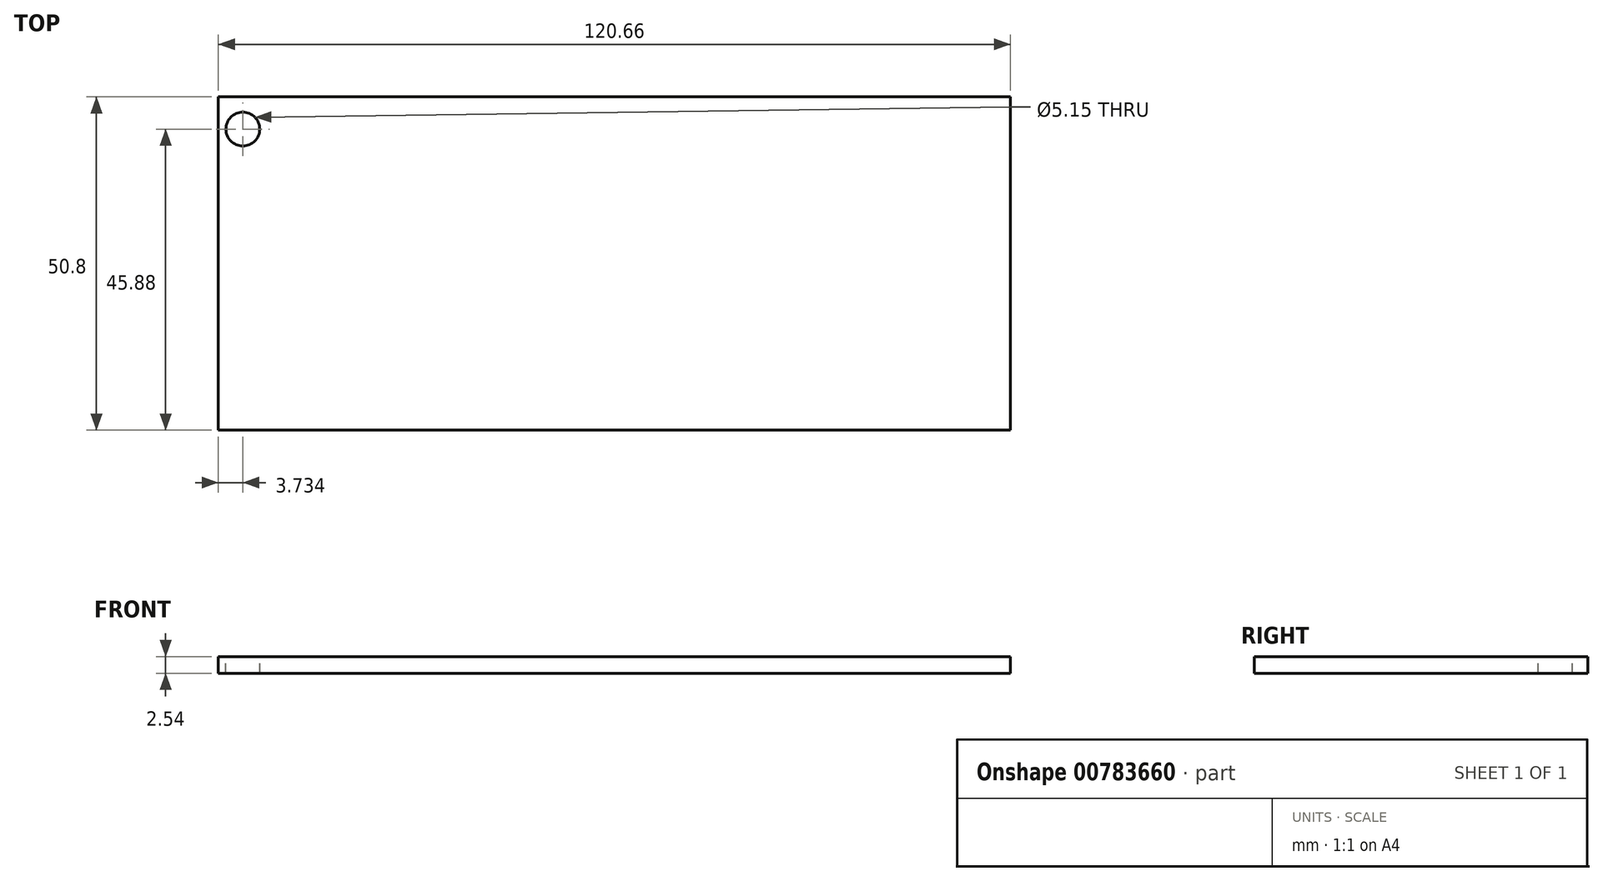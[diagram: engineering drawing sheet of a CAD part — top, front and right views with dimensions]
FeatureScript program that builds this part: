
annotation { "Feature Type Name" : "Feature", "Feature Type Description" : "" }
export const myFeature = defineFeature(function(context is Context, id is Id, definition is map)
    precondition{}
    {
        {
            var Q0;
            Q0=qCreatedBy(makeId("Top.planeOp"),FACE);
            var sketch = newSketch(context, id + "F0", { "sketchPlane" : qUnion([Q0])});
            skLineSegment(sketch, "E0.bottom", {"start": v(-96.58, 50.8) * mm, "end": v(24.08, 50.8) * mm});
            skLineSegment(sketch, "E0.top", {"start": v(-96.58, 0) * mm, "end": v(24.08, 0) * mm});
            skLineSegment(sketch, "E0.left", {"start": v(-96.58, 50.8) * mm, "end": v(-96.58, 0) * mm});
            skLineSegment(sketch, "E0.right", {"start": v(24.08, 50.8) * mm, "end": v(24.08, 0) * mm});
            skSolve(sketch);
        }
        {
            var Q0;
            Q0 = qSketchRegion(id + "F0", true);
            extrude(context, id + "F1", {"entities" : qUnion([Q0]), "depth" : 2.54 * mm, "offsetDistance" : 25.4 * mm});
        }
        {
            var Q0;
            Q0=makeQuery(id+"F1.opExtrude","CAP_FACE",FACE,{"disambiguationData":[OSD([sQuery(id+"F0.wireOp",EDGE,"E0.bottom"),sQuery(id+"F0.wireOp",EDGE,"E0.top"),sQuery(id+"F0.wireOp",EDGE,"E0.left"),sQuery(id+"F0.wireOp",EDGE,"E0.right")])],"isStart":false});
            var sketch = newSketch(context, id + "F2", { "sketchPlane" : qUnion([Q0])});
            skCircle(sketch, "E1", {"center": v(-92.85, 45.88) * mm, "radius": 2.58 * mm});
            skSolve(sketch);
        }
        {
            var Q0;
            Q0 = qSketchRegion(id + "F2", true);
            extrude(context, id + "F3", {"entities" : qUnion([Q0]), "operationType" : NewBodyOperationType.REMOVE, "depth" : -5.08 * mm, "offsetDistance" : 25.4 * mm});
        }
    });
